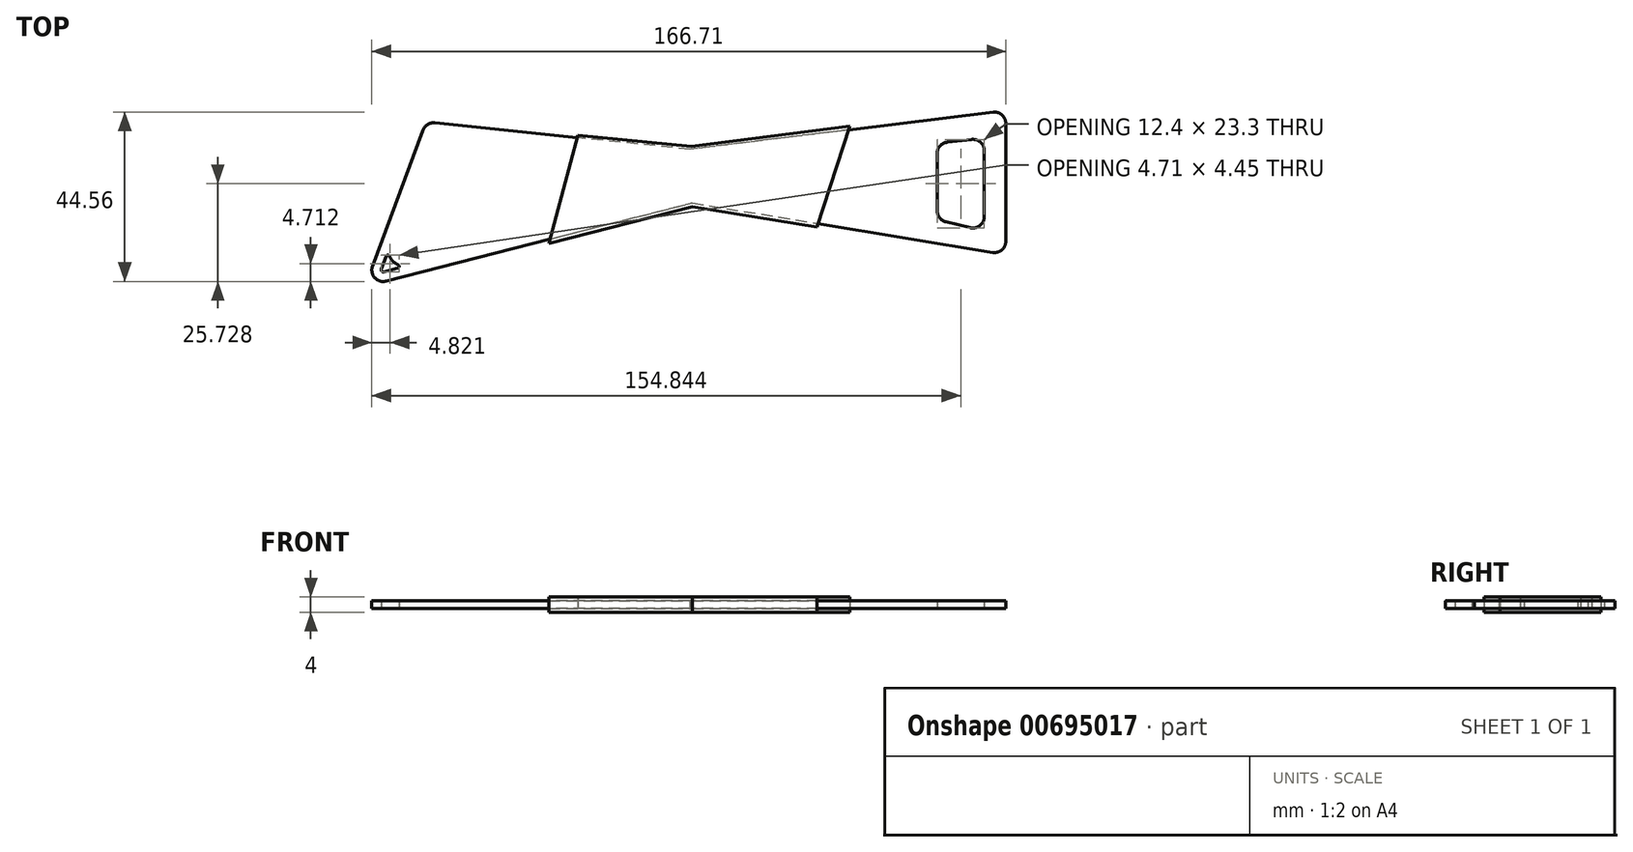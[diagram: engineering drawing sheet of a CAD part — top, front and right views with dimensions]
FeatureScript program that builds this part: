
annotation { "Feature Type Name" : "Feature", "Feature Type Description" : "" }
export const myFeature = defineFeature(function(context is Context, id is Id, definition is map)
    precondition{}
    {
        {
            var Q0;
            Q0=qCreatedBy(makeId("Top.planeOp"),FACE);
            var sketch = newSketch(context, id + "F0", { "sketchPlane" : qUnion([Q0])});
            skLineSegment(sketch, "E0", {"start": v(-85.05, -34.69) * mm, "end": v(-4.57, -14.09) * mm});
            skLineSegment(sketch, "E1", {"start": v(-4.57, -14.09) * mm, "end": v(74.42, -27.14) * mm});
            skLineSegment(sketch, "E2", {"start": v(77.91, -24.18) * mm, "end": v(77.91, 6.78) * mm});
            skLineSegment(sketch, "E3", {"start": v(74.55, 9.76) * mm, "end": v(-5.13, 0) * mm});
            skLineSegment(sketch, "E4", {"start": v(-5.13, 0) * mm, "end": v(-72.24, 6.95) * mm});
            skLineSegment(sketch, "E5", {"start": v(-75.36, 5) * mm, "end": v(-88.6, -30.74) * mm});
            skLineSegment(sketch, "E6", {"start": v(-86.3, -31.53) * mm, "end": v(-85.05, -28.17) * mm});
            skLineSegment(sketch, "E7", {"start": v(-85.62, -32.27) * mm, "end": v(-82, -31.27) * mm});
            skArc(sketch, "E8", {"start": v(-84.12, -28.15) * mm, "mid": v(-83.24, -29.45) * mm, "end": v(-81.93, -30.33) * mm});
            skPoint(sketch, "E9.visualSharp", {"position": v(-86.68, -32.56) * mm});
            skArc(sketch, "E9.filletArc", {"start": v(-86.3, -31.53) * mm, "mid": v(-86.19, -32.1) * mm, "end": v(-85.62, -32.27) * mm});
            skPoint(sketch, "E10.visualSharp", {"position": v(-84.46, -26.57) * mm});
            skArc(sketch, "E10.filletArc", {"start": v(-84.12, -28.15) * mm, "mid": v(-84.6, -27.84) * mm, "end": v(-85.05, -28.17) * mm});
            skPoint(sketch, "E11.visualSharp", {"position": v(-79.22, -30.51) * mm});
            skArc(sketch, "E11.filletArc", {"start": v(-82, -31.27) * mm, "mid": v(-81.63, -30.83) * mm, "end": v(-81.93, -30.33) * mm});
            skLineSegment(sketch, "E12", {"start": v(72.24, -17.7) * mm, "end": v(72.24, -0.39) * mm});
            skLineSegment(sketch, "E13", {"start": v(68.9, 2.6) * mm, "end": v(62.5, 1.86) * mm});
            skLineSegment(sketch, "E14", {"start": v(59.85, -1.12) * mm, "end": v(59.85, -16.16) * mm});
            skLineSegment(sketch, "E15", {"start": v(62.14, -19.08) * mm, "end": v(68.54, -20.62) * mm});
            skPoint(sketch, "E16.visualSharp", {"position": v(72.24, 2.97) * mm});
            skArc(sketch, "E16.filletArc", {"start": v(72.24, 2.41) * mm, "mid": v(72.07, 2.78) * mm, "end": v(71.69, 2.9) * mm});
            skArc(sketch, "E17.filletArc", {"start": v(72.24, -0.39) * mm, "mid": v(71.24, 1.85) * mm, "end": v(68.9, 2.6) * mm});
            skPoint(sketch, "E18.visualSharp", {"position": v(72.24, -21.5) * mm});
            skArc(sketch, "E18.filletArc", {"start": v(68.54, -20.62) * mm, "mid": v(71.1, -20.06) * mm, "end": v(72.24, -17.7) * mm});
            skPoint(sketch, "E19.visualSharp", {"position": v(59.85, -18.53) * mm});
            skArc(sketch, "E19.filletArc", {"start": v(59.85, -16.16) * mm, "mid": v(60.49, -18.02) * mm, "end": v(62.14, -19.08) * mm});
            skPoint(sketch, "E20.visualSharp", {"position": v(59.85, 1.56) * mm});
            skArc(sketch, "E20.filletArc", {"start": v(62.5, 1.86) * mm, "mid": v(60.6, 0.88) * mm, "end": v(59.85, -1.12) * mm});
            skPoint(sketch, "E21.visualSharp", {"position": v(77.91, 10.17) * mm});
            skArc(sketch, "E21.filletArc", {"start": v(77.91, 6.78) * mm, "mid": v(76.9, 9.03) * mm, "end": v(74.55, 9.76) * mm});
            skPoint(sketch, "E22.visualSharp", {"position": v(77.91, -27.71) * mm});
            skArc(sketch, "E22.filletArc", {"start": v(74.42, -27.14) * mm, "mid": v(76.85, -26.46) * mm, "end": v(77.91, -24.18) * mm});
            skPoint(sketch, "E23.visualSharp", {"position": v(-74.55, 7.18) * mm});
            skArc(sketch, "E23.filletArc", {"start": v(-72.24, 6.95) * mm, "mid": v(-74.13, 6.5) * mm, "end": v(-75.36, 5) * mm});
            skPoint(sketch, "E24.visualSharp", {"position": v(-90.6, -36.1) * mm});
            skArc(sketch, "E24.filletArc", {"start": v(-88.6, -30.74) * mm, "mid": v(-88.03, -33.8) * mm, "end": v(-85.05, -34.69) * mm});
            skSolve(sketch);
        }
        {
            var Q0;
            Q0=makeQuery(id+"F0.imprint","IMPRINT",FACE,{"disambiguationData":[TD([[makeQuery(id+"F0.imprint","IMPRINT",EDGE,{"derivedFrom":sQuery(id+"F0.wireOp",EDGE,"E0")}),1.0]])]});
            extrude(context, id + "F1", {"entities" : qUnion([Q0]), "depth" : 2 * mm, "offsetDistance" : 25 * mm});
        }
        {
            var Q0;
            Q0=qCreatedBy(makeId("Top.planeOp"),FACE);
            cPlane(context, id + "F2", {"entities" : qUnion([Q0]), "cplaneType" : CPlaneType.OFFSET, "offset" : 1 * mm, "oppositeDirection" : true, "width" : 150 * mm, "height" : 150 * mm});
        }
        {
            var Q0;
            Q0=qCreatedBy(id+"F2.planeOp",FACE);
            var sketch = newSketch(context, id + "F3", { "sketchPlane" : qUnion([Q0])});
            skLineSegment(sketch, "E25", {"start": v(-42.27, -24.71) * mm, "end": v(-4.53, -15.08) * mm});
            skLineSegment(sketch, "E26", {"start": v(-4.53, -15.08) * mm, "end": v(28.2, -20.5) * mm});
            skLineSegment(sketch, "E27", {"start": v(28.2, -20.5) * mm, "end": v(36.9, 6.03) * mm});
            skLineSegment(sketch, "E28", {"start": v(36.9, 6.03) * mm, "end": v(-4.71, 0.76) * mm});
            skLineSegment(sketch, "E29", {"start": v(-4.71, 0.76) * mm, "end": v(-34.6, 3.66) * mm});
            skLineSegment(sketch, "E30", {"start": v(-34.6, 3.66) * mm, "end": v(-42.27, -24.71) * mm});
            skSolve(sketch);
        }
        {
            var Q0;
            Q0=makeQuery(id+"F3.imprint","IMPRINT",FACE,{"disambiguationData":[TD([[makeQuery(id+"F3.imprint","IMPRINT",EDGE,{"derivedFrom":sQuery(id+"F3.wireOp",EDGE,"E25")}),1.0]])]});
            extrude(context, id + "F4", {"entities" : qUnion([Q0]), "depth" : 4 * mm, "offsetDistance" : 25 * mm});
        }
    });
